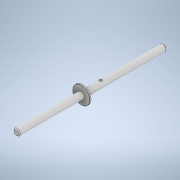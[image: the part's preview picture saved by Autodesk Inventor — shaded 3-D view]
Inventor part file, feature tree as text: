
AUTODESK INVENTOR PART (.ipt)
format: ipt  version: 2022 (Build 260153000, 153)  size: 125,952 bytes
history: native  units: mm
features: chamfer x2, sketch x2, revolve x1, extrude x1
ambient origin geometry x8: Origin, YZ Plane, XZ Plane, XY Plane, X Axis, Y Axis, Z Axis, Center Point
bodies: Solid1 (feature_tree)
feature tree (6):
  revolve  "Revolution1"  [1 undecoded]
  extrude  "Extrusion1"  Depth=150.0mm
  chamfer  "Chamfer1"  Distance=6.0mm
  chamfer  "Chamfer2"  Angle=90.0deg  [1 undecoded]
  sketch  "Sketch1"  dims[d0=120.0mm d1=3.0mm]
  sketch  "Sketch3"  dims[d2=10.0mm d3=150.0mm d4=6.0mm d5=90.0deg d6=5.0mm d7=33.0mm d8=10.0mm d9=0.0mm d10=2.0mm d11=2.0mm d12=45.0deg d13=0.5mm d14=2.0mm d15=45.0deg]
note: 2 required parameter values undecoded (feature->parameter linkage not recoverable at this tier; creation-order binding heuristic only, values carry confidence <= 0.55)